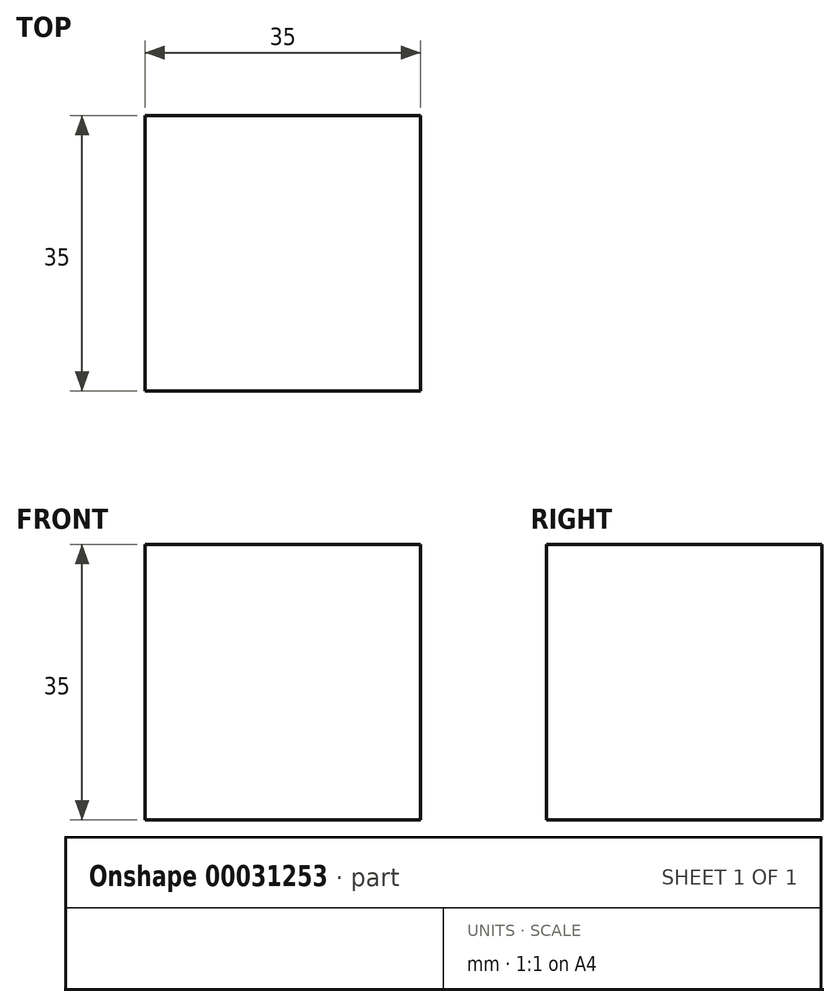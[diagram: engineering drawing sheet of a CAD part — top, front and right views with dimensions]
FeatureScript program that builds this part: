
annotation { "Feature Type Name" : "Feature", "Feature Type Description" : "" }
export const myFeature = defineFeature(function(context is Context, id is Id, definition is map)
    precondition{}
    {
        {
            var Q0;
            Q0=qCreatedBy(makeId("Top.planeOp"),FACE);
            var sketch = newSketch(context, id + "F0", { "sketchPlane" : qUnion([Q0])});
            skLineSegment(sketch, "E0.bottom", {"start": v(-17.5, 17.5) * mm, "end": v(17.5, 17.5) * mm});
            skLineSegment(sketch, "E0.top", {"start": v(-17.5, -17.5) * mm, "end": v(17.5, -17.5) * mm});
            skLineSegment(sketch, "E0.left", {"start": v(-17.5, 17.5) * mm, "end": v(-17.5, -17.5) * mm});
            skLineSegment(sketch, "E0.right", {"start": v(17.5, 17.5) * mm, "end": v(17.5, -17.5) * mm});
            skPoint(sketch, "E0.middle", {"position": v(0, 0) * mm});
            skSolve(sketch);
        }
        {
            var Q0;
            Q0 = qSketchRegion(id + "F0", true);
            extrude(context, id + "F1", {"entities" : qUnion([Q0]), "depth" : 35 * mm});
        }
    });
